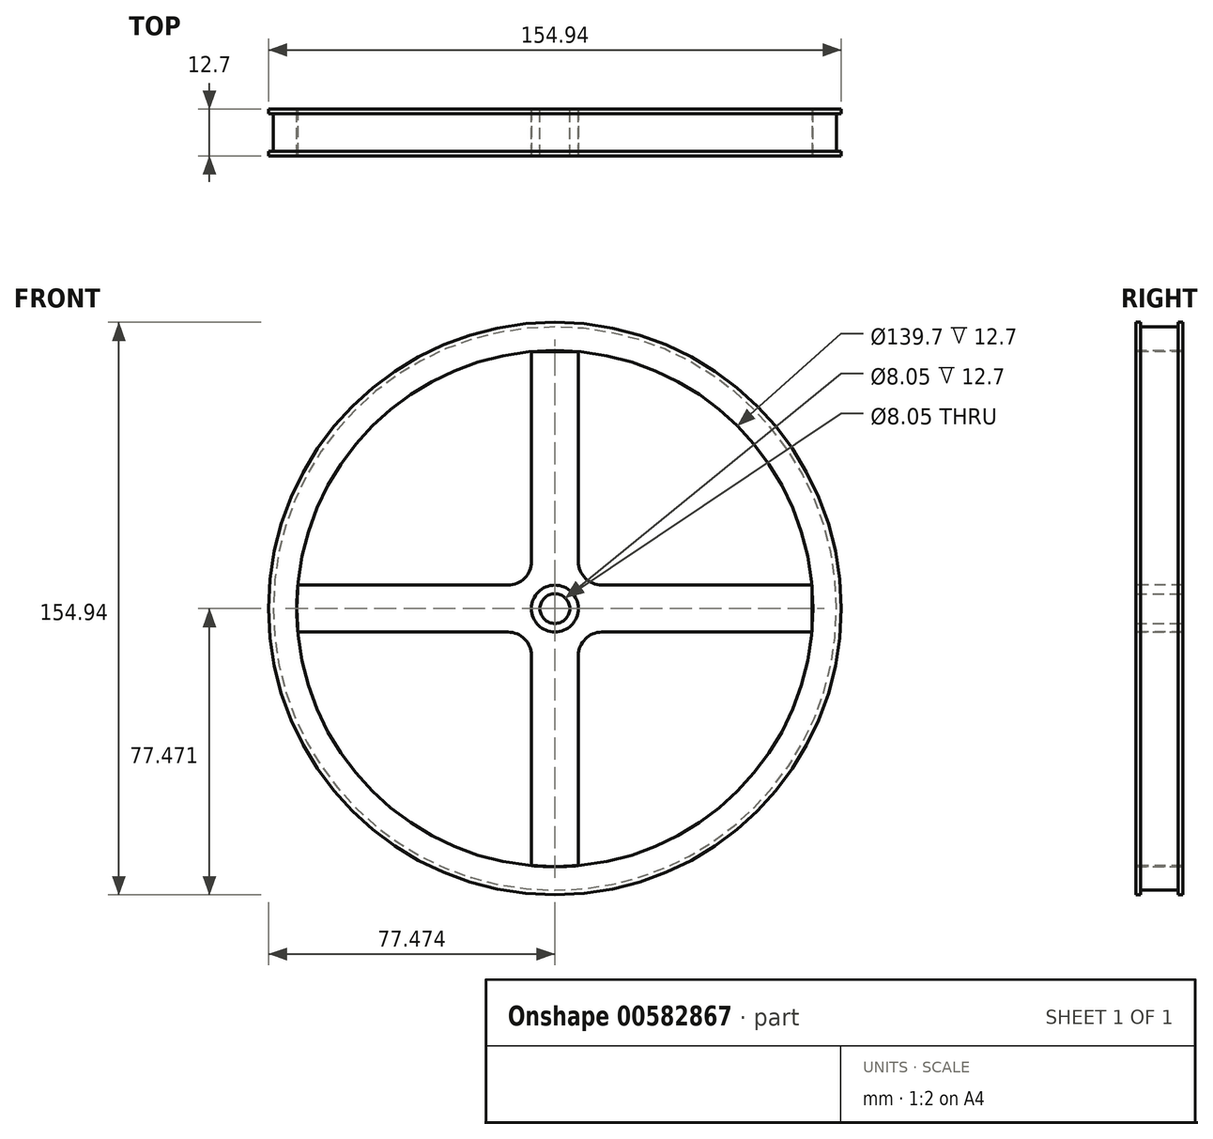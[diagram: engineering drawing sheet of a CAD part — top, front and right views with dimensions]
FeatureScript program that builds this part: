
annotation { "Feature Type Name" : "Feature", "Feature Type Description" : "" }
export const myFeature = defineFeature(function(context is Context, id is Id, definition is map)
    precondition{}
    {
        {
            var Q0;
            Q0=qCreatedBy(makeId("Front.planeOp"),FACE);
            var sketch = newSketch(context, id + "F0", { "sketchPlane" : qUnion([Q0])});
            skCircle(sketch, "E0", {"center": v(-22.45, 18.78) * mm, "radius": 76.2 * mm});
            skSolve(sketch);
        }
        {
            var Q0;
            Q0=makeQuery(id+"F0.imprint","IMPRINT",FACE,{"disambiguationData":[TD([[makeQuery(id+"F0.imprint","IMPRINT",EDGE,{"derivedFrom":sQuery(id+"F0.wireOp",EDGE,"E0")}),1.0]])]});
            var sketch = newSketch(context, id + "F1", { "sketchPlane" : qUnion([Q0])});
            skCircle(sketch, "E1", {"center": v(-22.45, 18.78) * mm, "radius": 69.85 * mm});
            skSolve(sketch);
        }
        {
            var Q0;
            Q0=makeQuery(id+"F0.imprint","IMPRINT",FACE,{"disambiguationData":[TD([[makeQuery(id+"F0.imprint","IMPRINT",EDGE,{"derivedFrom":sQuery(id+"F0.wireOp",EDGE,"E0")}),1.0]])]});
            extrude(context, id + "F2", {"entities" : qUnion([Q0]), "depth" : 12.7 * mm, "offsetDistance" : 25.4 * mm});
        }
        {
            var Q0;
            Q0=makeQuery(id+"F2.opExtrude","CAP_FACE",FACE,{"disambiguationData":[OSD([sQuery(id+"F0.wireOp",EDGE,"E0")])],"isStart":false});
            var sketch = newSketch(context, id + "F3", { "sketchPlane" : qUnion([Q0])});
            skCircle(sketch, "E2", {"center": v(-22.45, 18.78) * mm, "radius": 77.47 * mm});
            skSolve(sketch);
        }
        {
            var Q0;
            Q0 = qSketchRegion(id + "F3", true);
            extrude(context, id + "F4", {"entities" : qUnion([Q0]), "operationType" : NewBodyOperationType.ADD, "oppositeDirection" : true, "depth" : 1.27 * mm, "offsetDistance" : 25.4 * mm});
        }
        {
            var Q0;
            Q0=makeQuery(id+"F1.imprint","IMPRINT",FACE,{"disambiguationData":[TD([[makeQuery(id+"F1.imprint","IMPRINT",EDGE,{"derivedFrom":sQuery(id+"F1.wireOp",EDGE,"E1")}),-1.0]])]});
            var sketch = newSketch(context, id + "F5", { "sketchPlane" : qUnion([Q0])});
            skCircle(sketch, "E3", {"center": v(-22.45, 18.78) * mm, "radius": 77.47 * mm});
            skSolve(sketch);
        }
        {
            var Q0;
            Q0 = qSketchRegion(id + "F5", true);
            extrude(context, id + "F6", {"entities" : qUnion([Q0]), "operationType" : NewBodyOperationType.ADD, "depth" : 1.27 * mm, "offsetDistance" : 25.4 * mm});
        }
        {
            var Q0;
            Q0=makeQuery(id+"F1.imprint","IMPRINT",FACE,{"disambiguationData":[TD([[makeQuery(id+"F1.imprint","IMPRINT",EDGE,{"derivedFrom":sQuery(id+"F1.wireOp",EDGE,"E1")}),-1.0]])]});
            var sketch = newSketch(context, id + "F7", { "sketchPlane" : qUnion([Q0])});
            skCircle(sketch, "E4", {"center": v(-22.45, 18.78) * mm, "radius": 6.35 * mm});
            skCircle(sketch, "E5", {"center": v(-22.45, 18.78) * mm, "radius": 4.03 * mm});
            skSolve(sketch);
        }
        {
            var Q0;
            Q0=makeQuery(id+"F7.imprint","IMPRINT",FACE,{"disambiguationData":[TD([[makeQuery(id+"F7.imprint","IMPRINT",EDGE,{"derivedFrom":sQuery(id+"F7.wireOp",EDGE,"E5")}),1.0]])]});
            extrude(context, id + "F8", {"entities" : qUnion([Q0]), "operationType" : NewBodyOperationType.REMOVE, "depth" : 25.4 * mm, "offsetDistance" : 25.4 * mm});
        }
        {
            var Q0;
            Q0=sQuery(id+"F7.wireOp",EDGE,"E4");
            extrude(context, id + "F9", {"bodyType" : ToolBodyType.SURFACE, "surfaceEntities" : qUnion([Q0]), "depth" : 12.7 * mm, "offsetDistance" : 25.4 * mm});
        }
        {
            var Q0;
            Q0=makeQuery(id+"F1.imprint","IMPRINT",FACE,{"disambiguationData":[TD([[makeQuery(id+"F1.imprint","IMPRINT",EDGE,{"derivedFrom":sQuery(id+"F1.wireOp",EDGE,"E1")}),1.0]])]});
            var Q1;
            Q1=sQuery(id+"F1.wireOp",EDGE,"E1");
            extrude(context, id + "F10", {"entities" : qUnion([Q0]), "operationType" : NewBodyOperationType.REMOVE, "surfaceEntities" : qUnion([Q1]), "depth" : 25.4 * mm, "offsetDistance" : 25.4 * mm});
        }
        {
            var Q0;
            Q0=makeQuery(id+"F7.imprint","IMPRINT",FACE,{"disambiguationData":[TD([[makeQuery(id+"F7.imprint","IMPRINT",EDGE,{"derivedFrom":sQuery(id+"F7.wireOp",EDGE,"E4")}),-1.0]])]});
            var sketch = newSketch(context, id + "F11", { "sketchPlane" : qUnion([Q0])});
            skSolve(sketch);
        }
        {
            var Q0;
            Q0=makeQuery(id+"F11.imprint","IMPRINT",FACE,{"disambiguationData":[TD([[makeQuery(id+"F11.imprint","IMPRINT",EDGE,{"derivedFrom":makeQuery(id+"F7.imprint","IMPRINT",EDGE,{"derivedFrom":sQuery(id+"F7.wireOp",EDGE,"E4")})}),1.0]])]});
            var Q1;
            Q1=sQuery(id+"F7.wireOp",EDGE,"E4");
            extrude(context, id + "F12", {"entities" : qUnion([Q0]), "surfaceEntities" : qUnion([Q1]), "depth" : 12.7 * mm, "offsetDistance" : 25.4 * mm});
        }
        {
            var Q0;
            Q0=makeQuery(id+"F7.imprint","IMPRINT",FACE,{"disambiguationData":[TD([[makeQuery(id+"F7.imprint","IMPRINT",EDGE,{"derivedFrom":sQuery(id+"F7.wireOp",EDGE,"E5")}),1.0]])]});
            extrude(context, id + "F13", {"entities" : qUnion([Q0]), "operationType" : NewBodyOperationType.REMOVE, "depth" : 25.4 * mm, "offsetDistance" : 25.4 * mm});
        }
        {
            var Q0;
            Q0=makeQuery(id+"F4.boolean.opBoolean","MERGE",FACE,{"derivedFrom":[makeQuery(id+"F2.opExtrude","CAP_FACE",FACE,{"disambiguationData":[OSD([sQuery(id+"F0.wireOp",EDGE,"E0")])],"isStart":false}),makeQuery(id+"F4.opExtrude","CAP_FACE",FACE,{"disambiguationData":[OSD([sQuery(id+"F3.wireOp",EDGE,"E2")])],"isStart":true})]});
            var sketch = newSketch(context, id + "F14", { "sketchPlane" : qUnion([Q0])});
            skLineSegment(sketch, "E6", {"start": v(-16.08, -44.7) * mm, "end": v(-16.08, -50.78) * mm});
            skLineSegment(sketch, "E7", {"start": v(-16.08, -50.78) * mm, "end": v(-16.08, 6.08) * mm});
            skLineSegment(sketch, "E8", {"start": v(-16.08, 82.27) * mm, "end": v(-16.08, 88.34) * mm});
            skLineSegment(sketch, "E9", {"start": v(-16.08, 88.34) * mm, "end": v(-28.79, 88.34) * mm});
            skLineSegment(sketch, "E10", {"start": v(-28.79, 88.34) * mm, "end": v(-28.79, 31.48) * mm});
            skLineSegment(sketch, "E11", {"start": v(-28.79, -50.78) * mm, "end": v(-28.79, 6.08) * mm});
            skLineSegment(sketch, "E12", {"start": v(-9.73, 12.43) * mm, "end": v(47.12, 12.43) * mm});
            skLineSegment(sketch, "E13", {"start": v(47.12, 12.43) * mm, "end": v(47.12, 25.13) * mm});
            skLineSegment(sketch, "E14", {"start": v(47.12, 25.13) * mm, "end": v(-9.73, 25.13) * mm});
            skLineSegment(sketch, "E15", {"start": v(-35.14, 12.43) * mm, "end": v(-92, 12.43) * mm});
            skArc(sketch, "E16.filletArc", {"start": v(-28.79, 6.08) * mm, "mid": v(-30.65, 10.57) * mm, "end": v(-35.14, 12.43) * mm});
            skArc(sketch, "E17.filletArc", {"start": v(-9.73, 12.43) * mm, "mid": v(-14.22, 10.57) * mm, "end": v(-16.08, 6.08) * mm});
            skLineSegment(sketch, "E18", {"start": v(-16.08, 31.48) * mm, "end": v(-16.08, 82.27) * mm});
            skArc(sketch, "E19.filletArc", {"start": v(-16.08, 31.48) * mm, "mid": v(-14.22, 27) * mm, "end": v(-9.73, 25.13) * mm});
            skLineSegment(sketch, "E20", {"start": v(-35.14, 25.13) * mm, "end": v(-92, 25.13) * mm});
            skPoint(sketch, "E21.newPointA", {"position": v(-28.79, 25.13) * mm});
            skPoint(sketch, "E21.newPointB", {"position": v(-28.79, 18.78) * mm});
            skArc(sketch, "E21.filletArc", {"start": v(-35.14, 25.13) * mm, "mid": v(-30.65, 27) * mm, "end": v(-28.79, 31.48) * mm});
            skSolve(sketch);
        }
        {
            var Q0;
            Q0 = qSketchRegion(id + "F14", true);
            var Q1;
            Q1=makeQuery(id+"F14.imprint","IMPRINT",FACE,{"disambiguationData":[TD([[makeQuery(id+"F14.imprint","IMPRINT",EDGE,{"derivedFrom":sQuery(id+"F14.wireOp",EDGE,"E8")}),1.0]])]});
            extrude(context, id + "F15", {"entities" : qUnion([Q0, Q1]), "oppositeDirection" : true, "depth" : 12.7 * mm, "offsetDistance" : 25.4 * mm});
        }
        {
            var Q0;
            Q0=makeQuery(id+"F7.imprint","IMPRINT",FACE,{"disambiguationData":[TD([[makeQuery(id+"F7.imprint","IMPRINT",EDGE,{"derivedFrom":sQuery(id+"F7.wireOp",EDGE,"E5")}),1.0]])]});
            extrude(context, id + "F16", {"entities" : qUnion([Q0]), "operationType" : NewBodyOperationType.REMOVE, "depth" : 25.4 * mm, "offsetDistance" : 25.4 * mm});
        }
    });
